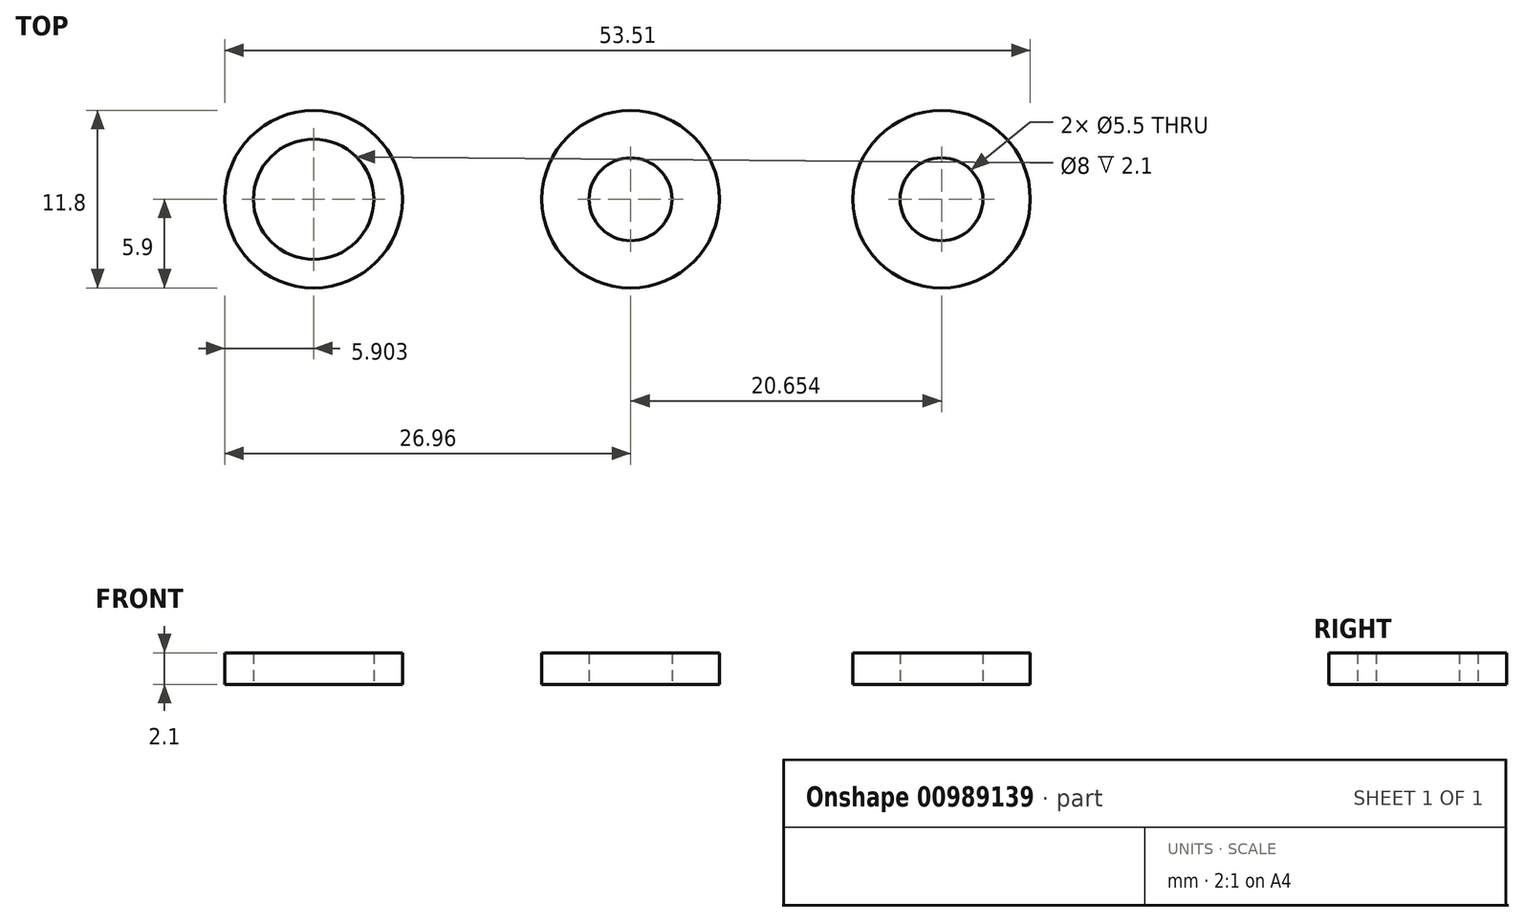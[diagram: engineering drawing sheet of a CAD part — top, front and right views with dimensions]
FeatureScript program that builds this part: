
annotation { "Feature Type Name" : "Feature", "Feature Type Description" : "" }
export const myFeature = defineFeature(function(context is Context, id is Id, definition is map)
    precondition{}
    {
        {
            var Q0;
            Q0=qCreatedBy(makeId("Top.planeOp"),FACE);
            var sketch = newSketch(context, id + "F0", { "sketchPlane" : qUnion([Q0])});
            skCircle(sketch, "E0", {"center": v(0, 0) * mm, "radius": 5.9 * mm});
            skCircle(sketch, "E1", {"center": v(0, 0) * mm, "radius": 2.75 * mm});
            skCircle(sketch, "E2", {"center": v(20.65, 0) * mm, "radius": 5.9 * mm});
            skCircle(sketch, "E3", {"center": v(20.65, 0) * mm, "radius": 2.75 * mm});
            skCircle(sketch, "E4", {"center": v(-21.06, 0) * mm, "radius": 5.9 * mm});
            skCircle(sketch, "E5", {"center": v(-21.06, 0) * mm, "radius": 4 * mm});
            skSolve(sketch);
        }
        {
            var Q0;
            Q0=makeQuery(id+"F0.imprint","IMPRINT",FACE,{"disambiguationData":[TD([[makeQuery(id+"F0.imprint","IMPRINT",EDGE,{"derivedFrom":sQuery(id+"F0.wireOp",EDGE,"E0")}),1.0]])]});
            var Q1;
            Q1=makeQuery(id+"F0.imprint","IMPRINT",FACE,{"disambiguationData":[TD([[makeQuery(id+"F0.imprint","IMPRINT",EDGE,{"derivedFrom":sQuery(id+"F0.wireOp",EDGE,"E4")}),1.0]])]});
            var Q2;
            Q2=makeQuery(id+"F0.imprint","IMPRINT",FACE,{"disambiguationData":[TD([[makeQuery(id+"F0.imprint","IMPRINT",EDGE,{"derivedFrom":sQuery(id+"F0.wireOp",EDGE,"E2")}),1.0]])]});
            extrude(context, id + "F1", {"entities" : qUnion([Q0, Q1, Q2]), "depth" : 2.1 * mm, "offsetDistance" : 25.4 * mm});
        }
    });
